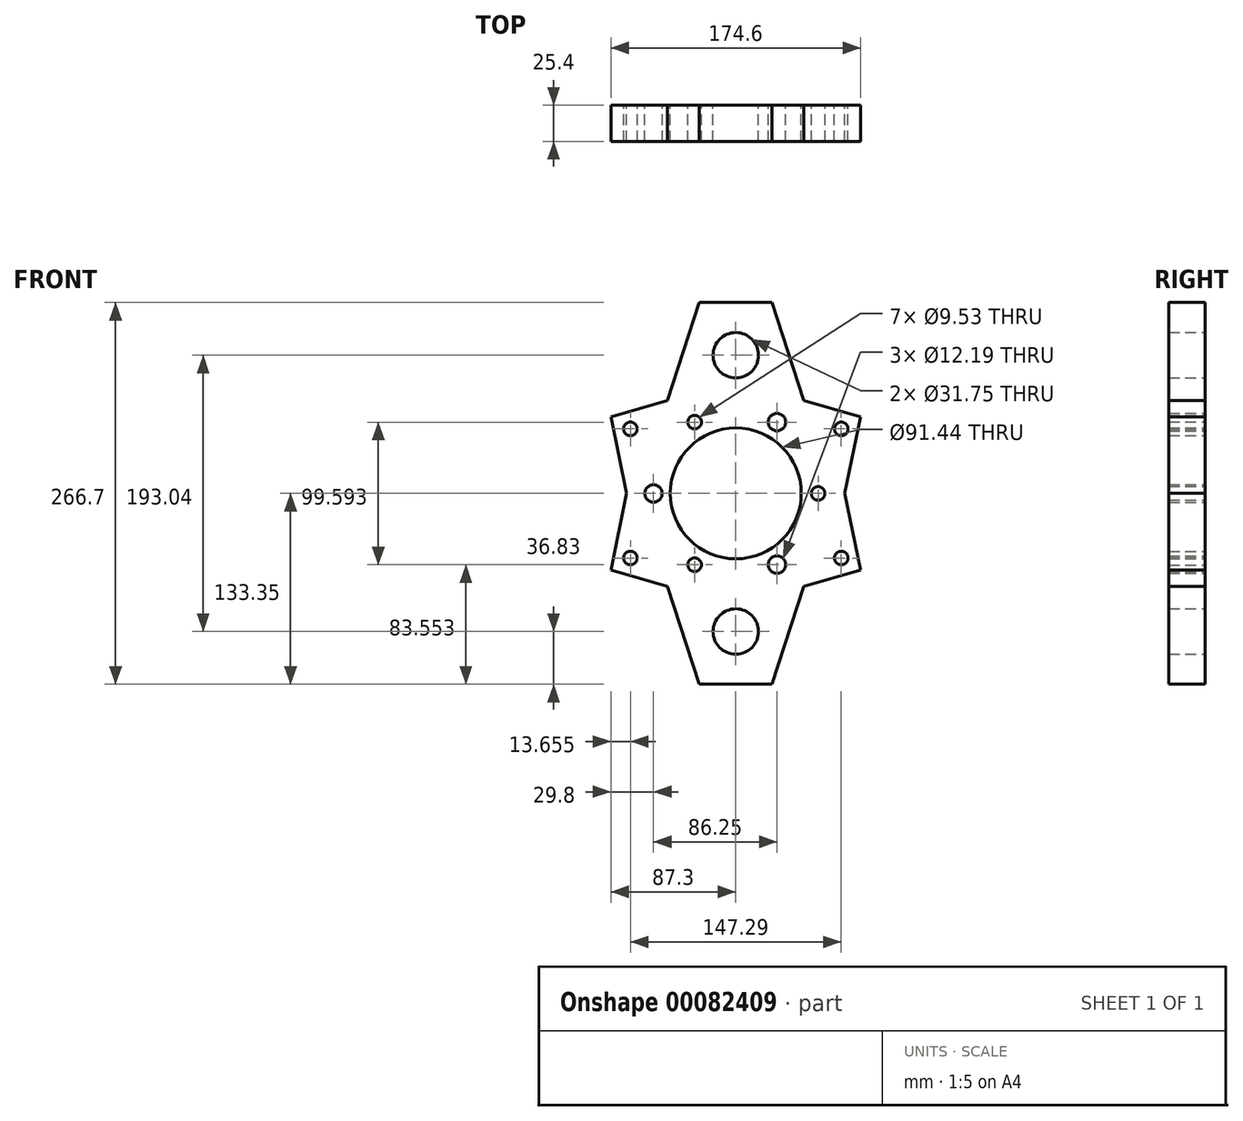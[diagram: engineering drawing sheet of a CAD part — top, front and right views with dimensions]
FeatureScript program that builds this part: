
annotation { "Feature Type Name" : "Feature", "Feature Type Description" : "" }
export const myFeature = defineFeature(function(context is Context, id is Id, definition is map)
    precondition{}
    {
        {
            var Q0;
            Q0=qCreatedBy(makeId("Front.planeOp"),FACE);
            var sketch = newSketch(context, id + "F0", { "sketchPlane" : qUnion([Q0])});
            skCircle(sketch, "E0", {"center": v(0, 0) * mm, "radius": 45.72 * mm});
            skCircle(sketch, "E1.cCircle", {"center": v(0, 0) * mm, "radius": 57.5 * mm, "construction": true});
            skCircle(sketch, "E2", {"center": v(28.75, 49.8) * mm, "radius": 6.1 * mm});
            skCircle(sketch, "E3", {"center": v(-57.5, 0) * mm, "radius": 6.1 * mm});
            skCircle(sketch, "E4", {"center": v(28.75, -49.8) * mm, "radius": 6.1 * mm});
            skCircle(sketch, "E5", {"center": v(-28.75, 49.8) * mm, "radius": 4.76 * mm});
            skCircle(sketch, "E6", {"center": v(57.5, 0) * mm, "radius": 4.76 * mm});
            skCircle(sketch, "E7", {"center": v(-28.75, -49.8) * mm, "radius": 4.76 * mm});
            skLineSegment(sketch, "E8", {"start": v(-76.2, 0) * mm, "end": v(-87.3, 53.47) * mm});
            skLineSegment(sketch, "E9", {"start": v(87.3, -53.47) * mm, "end": v(76.2, 0) * mm});
            skLineSegment(sketch, "E10", {"start": v(76.2, 0) * mm, "end": v(87.3, 53.47) * mm});
            skLineSegment(sketch, "E11", {"start": v(-76.2, 0) * mm, "end": v(-87.3, -53.47) * mm});
            skLineSegment(sketch, "E12.bottom", {"start": v(25.4, 133.35) * mm, "end": v(-25.4, 133.35) * mm});
            skLineSegment(sketch, "E12.top", {"start": v(25.4, -133.35) * mm, "end": v(-25.4, -133.35) * mm});
            skLineSegment(sketch, "E13", {"start": v(-25.4, 133.35) * mm, "end": v(-47.63, 64.84) * mm});
            skLineSegment(sketch, "E14", {"start": v(-47.63, 64.84) * mm, "end": v(-87.3, 53.47) * mm});
            skLineSegment(sketch, "E15", {"start": v(87.3, 53.47) * mm, "end": v(47.63, 64.84) * mm});
            skLineSegment(sketch, "E16", {"start": v(47.63, 64.84) * mm, "end": v(25.4, 133.35) * mm});
            skLineSegment(sketch, "E17", {"start": v(87.3, -53.47) * mm, "end": v(47.63, -64.84) * mm});
            skLineSegment(sketch, "E18", {"start": v(47.63, -64.84) * mm, "end": v(25.4, -133.35) * mm});
            skLineSegment(sketch, "E19", {"start": v(-25.4, -133.35) * mm, "end": v(-47.63, -64.84) * mm});
            skLineSegment(sketch, "E20", {"start": v(-47.62, -64.84) * mm, "end": v(-87.3, -53.47) * mm});
            skCircle(sketch, "E21", {"center": v(0, 96.52) * mm, "radius": 15.88 * mm});
            skCircle(sketch, "E22", {"center": v(0, -96.52) * mm, "radius": 15.88 * mm});
            skCircle(sketch, "E23", {"center": v(-73.65, 45.1) * mm, "radius": 4.76 * mm});
            skCircle(sketch, "E24", {"center": v(73.65, 45.1) * mm, "radius": 4.76 * mm});
            skCircle(sketch, "E25", {"center": v(73.65, -45.1) * mm, "radius": 4.76 * mm});
            skCircle(sketch, "E26", {"center": v(-73.64, -45.1) * mm, "radius": 4.76 * mm});
            skSolve(sketch);
        }
        {
            var Q0;
            Q0=makeQuery(id+"F0.imprint","IMPRINT",FACE,{"disambiguationData":[TD([[makeQuery(id+"F0.imprint","IMPRINT",EDGE,{"derivedFrom":sQuery(id+"F0.wireOp",EDGE,"E0")}),-1.0]])]});
            var sketch = newSketch(context, id + "F1", { "sketchPlane" : qUnion([Q0])});
            skSolve(sketch);
        }
        {
            var Q0;
            Q0=makeQuery(id+"F1.imprint","IMPRINT",FACE,{"disambiguationData":[TD([[makeQuery(id+"F1.imprint","IMPRINT",EDGE,{"derivedFrom":makeQuery(id+"F0.imprint","IMPRINT",EDGE,{"derivedFrom":sQuery(id+"F0.wireOp",EDGE,"E0")})}),-1.0]])]});
            extrude(context, id + "F2", {"entities" : qUnion([Q0]), "depth" : 25.4 * mm, "offsetDistance" : 25.4 * mm});
        }
    });
